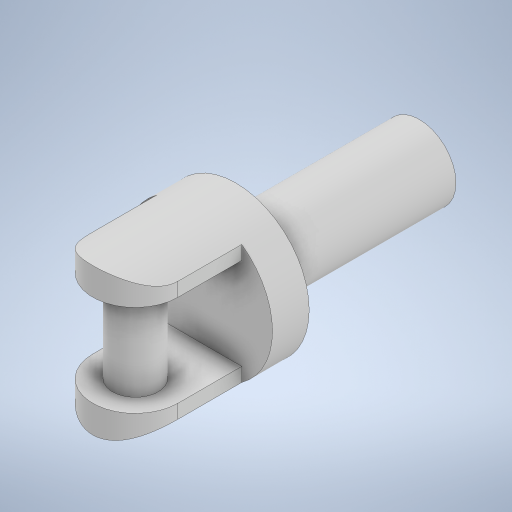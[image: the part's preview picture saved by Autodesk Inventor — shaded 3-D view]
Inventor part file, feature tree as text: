
AUTODESK INVENTOR PART (.ipt)
format: ipt  version: 2023 (Build 270158000, 158)  size: 295,424 bytes
history: native  units: in
note: dims shown in document units (in); Inventor stores cm internally (conversion verified against a paired STEP export)
features: sketch x5, extrude x4, revolve x1
ambient origin geometry x8: Origin, YZ Plane, XZ Plane, XY Plane, X Axis, Y Axis, Z Axis, Center Point
bodies: Solid1 (feature_tree)
feature tree (10):
  extrude  "Extrusion1"  Depth=2.0in TaperAngle=0.0deg
  revolve  "Revolution1"  [1 undecoded]
  extrude  "Extrusion2"  TaperAngle=90.0deg  [1 undecoded]
  extrude  "Extrusion3"  Depth=3.0in
  extrude  "Extrusion4"  Depth=10.0in TaperAngle=0.0deg
  sketch  "Sketch1"  dims[d0=2.0in d1=1.0in d2=0.0in]
  sketch  "Sketch2"  dims[d3=4.0in d4=0.0in d8=2.0in]
  sketch  "Sketch3"  dims[d9=4.0in d10=90.0deg]
  sketch  "Sketch4"  dims[d11=0.0in d12=3.0in]
  sketch  "Sketch5"  dims[d13=2.5in d14=10.0in d15=0.0in d16=0.4in d17=0.4in d19=10.0in d20=0.0in d21=1.25in d22=10.0in d23=0.0in d24=0.1in d25=0.5in d26=0.0344in d27=0.5in d28=0.0344in]
note: 2 required parameter values undecoded (feature->parameter linkage not recoverable at this tier; creation-order binding heuristic only, values carry confidence <= 0.55)